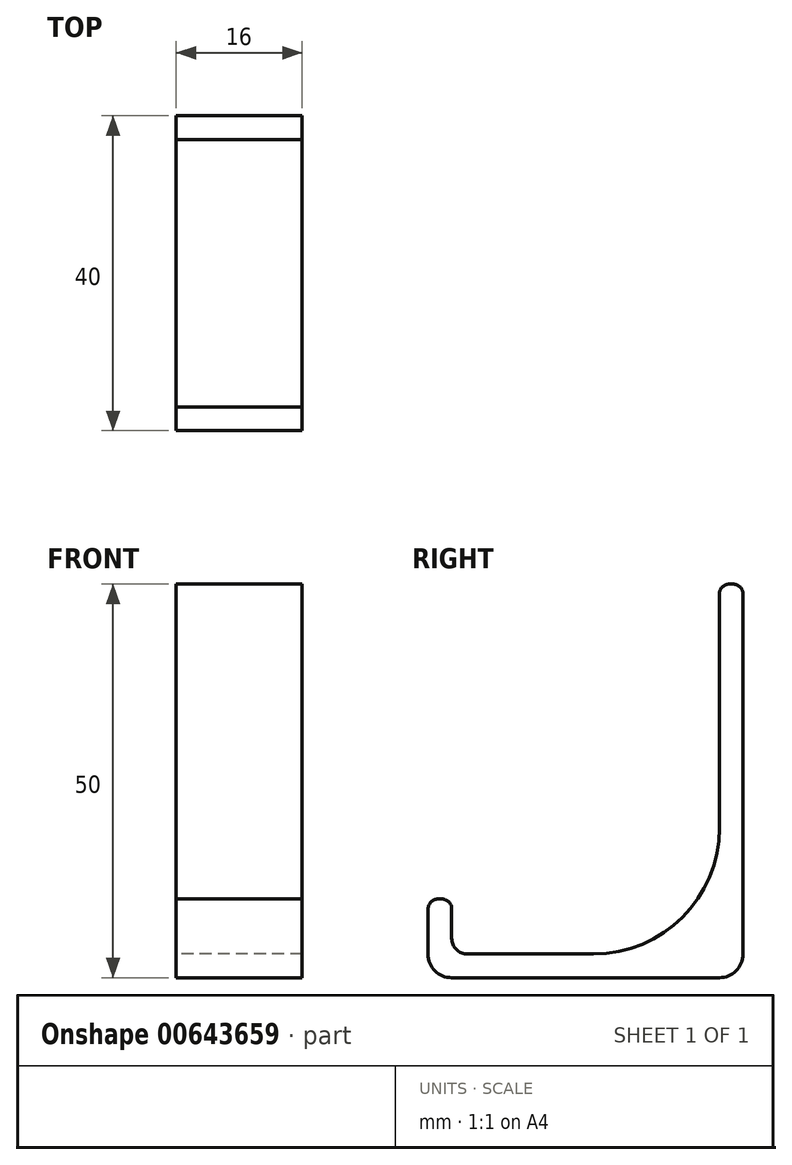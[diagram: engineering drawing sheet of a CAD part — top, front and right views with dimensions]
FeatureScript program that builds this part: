
annotation { "Feature Type Name" : "Feature", "Feature Type Description" : "" }
export const myFeature = defineFeature(function(context is Context, id is Id, definition is map)
    precondition{}
    {
        {
            var Q0;
            Q0=qCreatedBy(makeId("Right.planeOp"),FACE);
            var sketch = newSketch(context, id + "F0", { "sketchPlane" : qUnion([Q0])});
            skLineSegment(sketch, "E0", {"start": v(0, 0) * mm, "end": v(0, -47) * mm});
            skLineSegment(sketch, "E1", {"start": v(-3, -50) * mm, "end": v(-37, -50) * mm});
            skLineSegment(sketch, "E2", {"start": v(-40, -47) * mm, "end": v(-40, -40) * mm});
            skPoint(sketch, "E3.visualSharp", {"position": v(0, -50) * mm});
            skArc(sketch, "E3.filletArc", {"start": v(-3, -50) * mm, "mid": v(-0.88, -49.12) * mm, "end": v(0, -47) * mm});
            skPoint(sketch, "E4.visualSharp", {"position": v(-40, -50) * mm});
            skArc(sketch, "E4.filletArc", {"start": v(-40, -47) * mm, "mid": v(-39.12, -49.12) * mm, "end": v(-37, -50) * mm});
            skLineSegment(sketch, "E5.0", {"start": v(-37, -45) * mm, "end": v(-37, -40) * mm});
            skLineSegment(sketch, "E5.1", {"start": v(-19, -47) * mm, "end": v(-35, -47) * mm});
            skLineSegment(sketch, "E5.2", {"start": v(-3, 0) * mm, "end": v(-3, -31) * mm});
            skArc(sketch, "E6.filletArc", {"start": v(-37, -45) * mm, "mid": v(-36.41, -46.41) * mm, "end": v(-35, -47) * mm});
            skArc(sketch, "E7.filletArc", {"start": v(-19, -47) * mm, "mid": v(-7.69, -42.31) * mm, "end": v(-3, -31) * mm});
            skLineSegment(sketch, "E8", {"start": v(-37, -40) * mm, "end": v(-40, -40) * mm});
            skLineSegment(sketch, "E9", {"start": v(0, 0) * mm, "end": v(-3, 0) * mm});
            skSolve(sketch);
        }
        {
            var Q0;
            Q0=makeQuery(id+"F0.imprint","IMPRINT",FACE,{"disambiguationData":[TD([[makeQuery(id+"F0.imprint","IMPRINT",EDGE,{"derivedFrom":sQuery(id+"F0.wireOp",EDGE,"E0")}),-1.0]])]});
            extrude(context, id + "F1", {"entities" : qUnion([Q0]), "depth" : 16 * mm, "offsetDistance" : 25 * mm});
        }
        {
            var Q0;
            Q0=makeQuery(id+"F1.opExtrude","SWEPT_EDGE",EDGE,{"disambiguationData":[OSD([sQuery(id+"F0.wireOp",EDGE,"E0"),sQuery(id+"F0.wireOp",EDGE,"E9")])]});
            var Q1;
            Q1=makeQuery(id+"F1.opExtrude","SWEPT_EDGE",EDGE,{"disambiguationData":[OSD([sQuery(id+"F0.wireOp",EDGE,"E5.2"),sQuery(id+"F0.wireOp",EDGE,"E9")])]});
            fillet(context, id + "F2", {"entities" : qUnion([Q0, Q1]), "radius" : 1.25 * mm, "tangentPropagation" : true, "allowEdgeOverflow" : false});
        }
        {
            var Q0;
            Q0=makeQuery(id+"F1.opExtrude","SWEPT_EDGE",EDGE,{"disambiguationData":[OSD([sQuery(id+"F0.wireOp",EDGE,"E5.0"),sQuery(id+"F0.wireOp",EDGE,"E8")])]});
            var Q1;
            Q1=makeQuery(id+"F1.opExtrude","SWEPT_EDGE",EDGE,{"disambiguationData":[OSD([sQuery(id+"F0.wireOp",EDGE,"E2"),sQuery(id+"F0.wireOp",EDGE,"E8")])]});
            fillet(context, id + "F3", {"entities" : qUnion([Q0, Q1]), "radius" : 1.25 * mm, "tangentPropagation" : true, "allowEdgeOverflow" : false});
        }
    });
